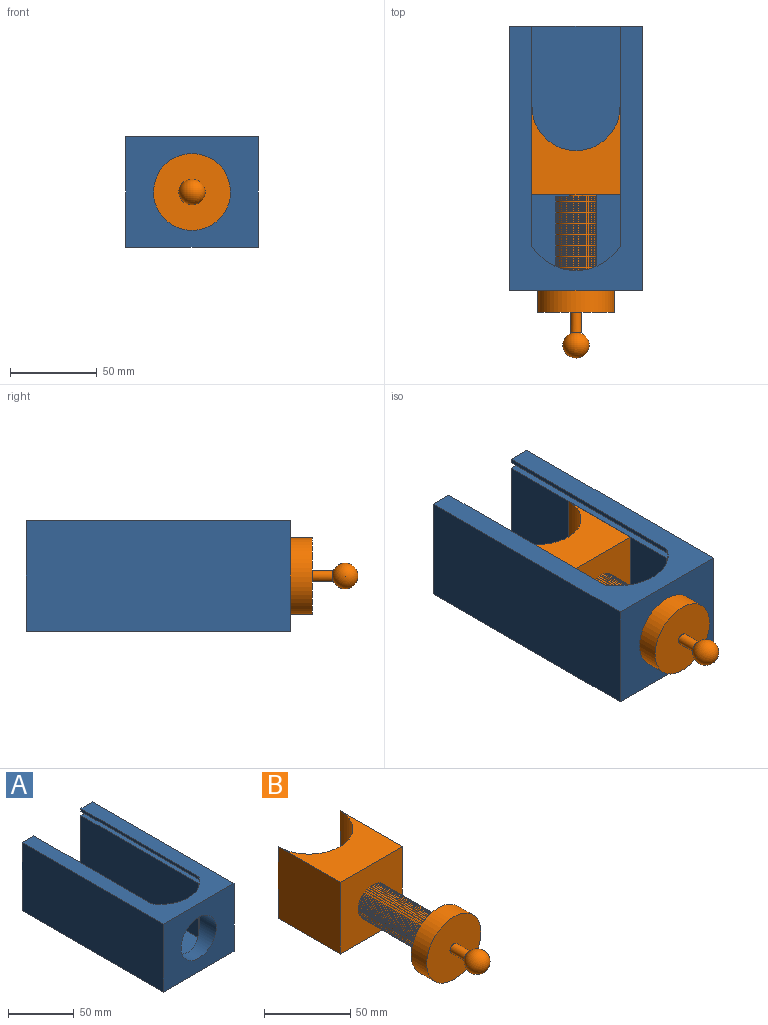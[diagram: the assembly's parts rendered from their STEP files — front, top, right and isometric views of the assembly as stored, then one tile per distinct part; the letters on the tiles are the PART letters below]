
ASSEMBLY  parts=2 mates=1
PART A: 19 faces, bbox 76.2x152.4x63.5 mm
  f0: plane 76.2x63.5mm, normal (0,1,0), area 1886.4mm2, adj f1,f3,f4,f6,f7,f8,f9,f11
  f1: plane 127x2.54mm, normal (1,0,0), area 322.6mm2, adj f0,f2,f4,f17
  f2: cylinder r=29.87mm len=50.8mm, axis (0,0,1), area 154.3mm2, adj f1,f3,f4,f17
  f3: plane 127x2.54mm, normal (-1,0,0), area 322.6mm2, adj f0,f2,f4,f17
  f4: plane 152.4x76.2mm, normal (0,0,1), area 4653.4mm2, adj f0,f1,f2,f3,f5,f6,f7
  f5: plane 76.2x63.5mm, normal (0,-1,0), area 3698.6mm2, adj f4,f6,f7,f8,f13
  f6: plane 152.4x63.5mm, normal (1,0,0), area 9677.4mm2, adj f0,f4,f5,f8
  f7: plane 152.4x63.5mm, normal (-1,0,0), area 9677.4mm2, adj f0,f4,f5,f8
  f8: plane 152.4x76.2mm, normal (0,0,-1), area 11612.9mm2, adj f0,f5,f6,f7
  f9: plane 127x50.75mm, normal (1,0,0), area 6444.9mm2, adj f0,f10,f12,f15
  f10: cylinder r=29.87mm len=50.8mm, axis (0,0,1), area 1874mm2, adj f9,f11,f12,f13,f15
  f11: plane 127x50.75mm, normal (-1,0,0), area 6444.9mm2, adj f0,f10,f12,f15
  f12: plane 141.15x50.8mm, normal (0,0,1), area 6959.5mm2, adj f0,f9,f10,f11
  f13: cylinder r=19.05mm len=38.1mm, axis (0,-1,0), area 1743.5mm2, adj f5,f10
  f14: plane 145.03x3.86mm, normal (-1,0,0), area 560.2mm2, adj f0,f15,f17,f18
  f15: plane 145.03x63.5mm, normal (0,0,1), area 2250.2mm2, adj f0,f9,f10,f11,f14,f16,f18
  f16: plane 145.03x3.86mm, normal (1,0,0), area 560.2mm2, adj f0,f15,f17,f18
  f17: plane 145.03x63.5mm, normal (0,0,-1), area 2250.2mm2, adj f0,f1,f2,f3,f14,f16,f18
  f18: plane 63.5x3.86mm, normal (0,1,0), area 245.3mm2, adj f14,f15,f16,f17
PART B: 189 faces, bbox 50.8x137.7x50.8 mm
  f0: plane 55.12x7.77mm, normal (0,0,1), area 390.6mm2, adj f1,f2,f3,f4,f5,f6,f7,f8
  f1: plane 23.16x23.16mm, normal (0,1,0), area 81.9mm2, adj f0,f132,f133,f134
  f2: plane 55.12x4.13mm, normal (1,0,0), area 227.7mm2, adj f0,f3,f133,f134,f135,f136,f137,f138
  f3: plane 50.8x50.8mm, normal (0,-1,0), area 2498.6mm2, adj f0,f2,f4,f134,f178,f179,f180,f181
  f4: cylinder r=3.81mm len=55.12mm, axis (0,-1,0), area 989.6mm2, adj f0,f3,f5,f178
  f5: plane 20.62x20.62mm, normal (0,1,0), area 258.4mm2, adj f0,f4,f6,f134,f178
  f6: cylinder r=10.31mm len=20.62mm, axis (0,1,0), area 41.8mm2, adj f0,f5,f7,f134
  f7: plane 23.16x23.16mm, normal (0,1,0), area 81.9mm2, adj f0,f6,f134,f176
  f8: plane 23.16x23.16mm, normal (0,-1,0), area 81.9mm2, adj f0,f9,f134,f175
  f9: cylinder r=10.31mm len=20.62mm, axis (0,1,0), area 41.8mm2, adj f0,f8,f10,f134
  f10: plane 23.16x23.16mm, normal (0,1,0), area 81.9mm2, adj f0,f9,f134,f175
  f11: plane 23.16x23.16mm, normal (0,-1,0), area 81.9mm2, adj f0,f12,f134,f174
  f12: cylinder r=10.31mm len=20.62mm, axis (0,1,0), area 41.8mm2, adj f0,f11,f13,f134
  f13: plane 23.16x23.16mm, normal (0,1,0), area 81.9mm2, adj f0,f12,f134,f174
  f14: plane 23.16x23.16mm, normal (0,-1,0), area 81.9mm2, adj f0,f15,f134,f173
  f15: cylinder r=10.31mm len=20.62mm, axis (0,1,0), area 41.8mm2, adj f0,f14,f16,f134
  f16: plane 23.16x23.16mm, normal (0,1,0), area 81.9mm2, adj f0,f15,f134,f173
  f17: plane 23.16x23.16mm, normal (0,-1,0), area 81.9mm2, adj f0,f18,f134,f172
  f18: cylinder r=10.31mm len=20.62mm, axis (0,1,0), area 41.8mm2, adj f0,f17,f19,f134
  f19: plane 23.16x23.16mm, normal (0,1,0), area 81.9mm2, adj f0,f18,f134,f172
  f20: plane 23.16x23.16mm, normal (0,-1,0), area 81.9mm2, adj f0,f21,f134,f171
  f21: cylinder r=10.31mm len=20.62mm, axis (0,1,0), area 41.8mm2, adj f0,f20,f22,f134
  f22: plane 23.16x23.16mm, normal (0,1,0), area 81.9mm2, adj f0,f21,f134,f171
  f23: plane 23.16x23.16mm, normal (0,-1,0), area 81.9mm2, adj f0,f24,f134,f170
  f24: cylinder r=10.31mm len=20.62mm, axis (0,1,0), area 41.8mm2, adj f0,f23,f25,f134
  f25: plane 23.16x23.16mm, normal (0,1,0), area 81.9mm2, adj f0,f24,f134,f170
  f26: plane 23.16x23.16mm, normal (0,-1,0), area 81.9mm2, adj f0,f27,f134,f169
  f27: cylinder r=10.31mm len=20.62mm, axis (0,1,0), area 41.8mm2, adj f0,f26,f28,f134
  f28: plane 23.16x23.16mm, normal (0,1,0), area 81.9mm2, adj f0,f27,f134,f169
  f29: plane 23.16x23.16mm, normal (0,-1,0), area 81.9mm2, adj f0,f30,f134,f168
  f30: cylinder r=10.31mm len=20.62mm, axis (0,1,0), area 41.8mm2, adj f0,f29,f31,f134
  f31: plane 23.16x23.16mm, normal (0,1,0), area 81.9mm2, adj f0,f30,f134,f168
  f32: plane 23.16x23.16mm, normal (0,-1,0), area 81.9mm2, adj f0,f33,f134,f167
  f33: cylinder r=10.31mm len=20.62mm, axis (0,1,0), area 41.8mm2, adj f0,f32,f34,f134
  f34: plane 23.16x23.16mm, normal (0,1,0), area 81.9mm2, adj f0,f33,f134,f167
  f35: plane 23.16x23.16mm, normal (0,-1,0), area 81.9mm2, adj f0,f36,f134,f166
  f36: cylinder r=10.31mm len=20.62mm, axis (0,1,0), area 41.8mm2, adj f0,f35,f37,f134
  f37: plane 23.16x23.16mm, normal (0,1,0), area 81.9mm2, adj f0,f36,f134,f166
  f38: plane 23.16x23.16mm, normal (0,-1,0), area 81.9mm2, adj f0,f39,f134,f165
  f39: cylinder r=10.31mm len=20.62mm, axis (0,1,0), area 41.8mm2, adj f0,f38,f40,f134
  f40: plane 23.16x23.16mm, normal (0,1,0), area 81.9mm2, adj f0,f39,f134,f165
  f41: plane 23.16x23.16mm, normal (0,-1,0), area 81.9mm2, adj f0,f42,f134,f164
  f42: cylinder r=10.31mm len=20.62mm, axis (0,1,0), area 41.8mm2, adj f0,f41,f43,f134
  f43: plane 23.16x23.16mm, normal (0,1,0), area 81.9mm2, adj f0,f42,f134,f164
  f44: plane 23.16x23.16mm, normal (0,-1,0), area 81.9mm2, adj f0,f45,f134,f163
  f45: cylinder r=10.31mm len=20.62mm, axis (0,1,0), area 41.8mm2, adj f0,f44,f46,f134
  f46: plane 23.16x23.16mm, normal (0,1,0), area 81.9mm2, adj f0,f45,f134,f163
  f47: plane 23.16x23.16mm, normal (0,-1,0), area 81.9mm2, adj f0,f48,f134,f162
  f48: cylinder r=10.31mm len=20.62mm, axis (0,1,0), area 41.8mm2, adj f0,f47,f49,f134
  f49: plane 23.16x23.16mm, normal (0,1,0), area 81.9mm2, adj f0,f48,f134,f162
  f50: plane 23.16x23.16mm, normal (0,-1,0), area 81.9mm2, adj f0,f51,f134,f161
  f51: cylinder r=10.31mm len=20.62mm, axis (0,1,0), area 41.8mm2, adj f0,f50,f52,f134
  f52: plane 23.16x23.16mm, normal (0,1,0), area 81.9mm2, adj f0,f51,f134,f161
  f53: plane 23.16x23.16mm, normal (0,-1,0), area 81.9mm2, adj f0,f54,f134,f160
  f54: cylinder r=10.31mm len=20.62mm, axis (0,1,0), area 41.8mm2, adj f0,f53,f55,f134
  f55: plane 23.16x23.16mm, normal (0,1,0), area 81.9mm2, adj f0,f54,f134,f160
  f56: plane 23.16x23.16mm, normal (0,-1,0), area 81.9mm2, adj f0,f57,f134,f159
  f57: cylinder r=10.31mm len=20.62mm, axis (0,1,0), area 41.8mm2, adj f0,f56,f58,f134
  f58: plane 23.16x23.16mm, normal (0,1,0), area 81.9mm2, adj f0,f57,f134,f159
  f59: plane 23.16x23.16mm, normal (0,-1,0), area 81.9mm2, adj f0,f60,f134,f158
  f60: cylinder r=10.31mm len=20.62mm, axis (0,1,0), area 41.8mm2, adj f0,f59,f61,f134
  f61: plane 23.16x23.16mm, normal (0,1,0), area 81.9mm2, adj f0,f60,f134,f158
  f62: plane 23.16x23.16mm, normal (0,-1,0), area 81.9mm2, adj f0,f63,f134,f157
  f63: cylinder r=10.31mm len=20.62mm, axis (0,1,0), area 41.8mm2, adj f0,f62,f64,f134
  f64: plane 23.16x23.16mm, normal (0,1,0), area 81.9mm2, adj f0,f63,f134,f157
  f65: plane 23.16x23.16mm, normal (0,-1,0), area 81.9mm2, adj f0,f66,f134,f156
  f66: cylinder r=10.31mm len=20.62mm, axis (0,1,0), area 41.8mm2, adj f0,f65,f67,f134
  f67: plane 23.16x23.16mm, normal (0,1,0), area 81.9mm2, adj f0,f66,f134,f156
  f68: plane 23.16x23.16mm, normal (0,-1,0), area 81.9mm2, adj f0,f69,f134,f155
  f69: cylinder r=10.31mm len=20.62mm, axis (0,1,0), area 41.8mm2, adj f0,f68,f70,f134
  f70: plane 23.16x23.16mm, normal (0,1,0), area 81.9mm2, adj f0,f69,f134,f155
  f71: plane 23.16x23.16mm, normal (0,-1,0), area 81.9mm2, adj f0,f72,f134,f154
  f72: cylinder r=10.31mm len=20.62mm, axis (0,1,0), area 41.8mm2, adj f0,f71,f73,f134
  f73: plane 23.16x23.16mm, normal (0,1,0), area 81.9mm2, adj f0,f72,f134,f154
  f74: plane 23.16x23.16mm, normal (0,-1,0), area 81.9mm2, adj f0,f75,f134,f153
  f75: cylinder r=10.31mm len=20.62mm, axis (0,1,0), area 41.8mm2, adj f0,f74,f76,f134
  f76: plane 23.16x23.16mm, normal (0,1,0), area 81.9mm2, adj f0,f75,f134,f153
  f77: plane 23.16x23.16mm, normal (0,-1,0), area 81.9mm2, adj f0,f78,f134,f152
  f78: cylinder r=10.31mm len=20.62mm, axis (0,1,0), area 41.8mm2, adj f0,f77,f79,f134
  f79: plane 23.16x23.16mm, normal (0,1,0), area 81.9mm2, adj f0,f78,f134,f152
  f80: plane 23.16x23.16mm, normal (0,-1,0), area 81.9mm2, adj f0,f81,f134,f151
  f81: cylinder r=10.31mm len=20.62mm, axis (0,1,0), area 41.8mm2, adj f0,f80,f82,f134
  f82: plane 23.16x23.16mm, normal (0,1,0), area 81.9mm2, adj f0,f81,f134,f151
  f83: plane 23.16x23.16mm, normal (0,-1,0), area 81.9mm2, adj f0,f84,f134,f150
  f84: cylinder r=10.31mm len=20.62mm, axis (0,1,0), area 41.8mm2, adj f0,f83,f85,f134
  f85: plane 23.16x23.16mm, normal (0,1,0), area 81.9mm2, adj f0,f84,f134,f150
  f86: plane 23.16x23.16mm, normal (0,-1,0), area 81.9mm2, adj f0,f87,f134,f149
  f87: cylinder r=10.31mm len=20.62mm, axis (0,1,0), area 41.8mm2, adj f0,f86,f88,f134
  f88: plane 23.16x23.16mm, normal (0,1,0), area 81.9mm2, adj f0,f87,f134,f149
  f89: plane 23.16x23.16mm, normal (0,-1,0), area 81.9mm2, adj f0,f90,f134,f148
  f90: cylinder r=10.31mm len=20.62mm, axis (0,1,0), area 41.8mm2, adj f0,f89,f91,f134
  f91: plane 23.16x23.16mm, normal (0,1,0), area 81.9mm2, adj f0,f90,f134,f148
  f92: plane 23.16x23.16mm, normal (0,-1,0), area 81.9mm2, adj f0,f93,f134,f147
  f93: cylinder r=10.31mm len=20.62mm, axis (0,1,0), area 41.8mm2, adj f0,f92,f94,f134
  f94: plane 23.16x23.16mm, normal (0,1,0), area 81.9mm2, adj f0,f93,f134,f147
  f95: plane 23.16x23.16mm, normal (0,-1,0), area 81.9mm2, adj f0,f96,f134,f146
  f96: cylinder r=10.31mm len=20.62mm, axis (0,1,0), area 41.8mm2, adj f0,f95,f97,f134
  f97: plane 23.16x23.16mm, normal (0,1,0), area 81.9mm2, adj f0,f96,f134,f146
  f98: plane 23.16x23.16mm, normal (0,-1,0), area 81.9mm2, adj f0,f99,f134,f145
  f99: cylinder r=10.31mm len=20.62mm, axis (0,1,0), area 41.8mm2, adj f0,f98,f100,f134
  f100: plane 23.16x23.16mm, normal (0,1,0), area 81.9mm2, adj f0,f99,f134,f145
  f101: plane 23.16x23.16mm, normal (0,-1,0), area 81.9mm2, adj f0,f102,f134,f144
  f102: cylinder r=10.31mm len=20.62mm, axis (0,1,0), area 41.8mm2, adj f0,f101,f103,f134
  f103: plane 23.16x23.16mm, normal (0,1,0), area 81.9mm2, adj f0,f102,f134,f144
  f104: plane 23.16x23.16mm, normal (0,-1,0), area 81.9mm2, adj f0,f105,f134,f143
  f105: cylinder r=10.31mm len=20.62mm, axis (0,1,0), area 41.8mm2, adj f0,f104,f106,f134
  f106: plane 23.16x23.16mm, normal (0,1,0), area 81.9mm2, adj f0,f105,f134,f143
  f107: plane 23.16x23.16mm, normal (0,-1,0), area 81.9mm2, adj f0,f108,f134,f142
  f108: cylinder r=10.31mm len=20.62mm, axis (0,1,0), area 41.8mm2, adj f0,f107,f109,f134
  f109: plane 23.16x23.16mm, normal (0,1,0), area 81.9mm2, adj f0,f108,f134,f142
  f110: plane 23.16x23.16mm, normal (0,-1,0), area 81.9mm2, adj f0,f111,f134,f141
  f111: cylinder r=10.31mm len=20.62mm, axis (0,1,0), area 41.8mm2, adj f0,f110,f112,f134
  f112: plane 23.16x23.16mm, normal (0,1,0), area 81.9mm2, adj f0,f111,f134,f141
  f113: plane 23.16x23.16mm, normal (0,-1,0), area 81.9mm2, adj f0,f114,f134,f140
  f114: cylinder r=10.31mm len=20.62mm, axis (0,1,0), area 41.8mm2, adj f0,f113,f115,f134
  f115: plane 23.16x23.16mm, normal (0,1,0), area 81.9mm2, adj f0,f114,f134,f140
  f116: plane 23.16x23.16mm, normal (0,-1,0), area 81.9mm2, adj f0,f117,f134,f139
  f117: cylinder r=10.31mm len=20.62mm, axis (0,1,0), area 41.8mm2, adj f0,f116,f118,f134
  f118: plane 23.16x23.16mm, normal (0,1,0), area 81.9mm2, adj f0,f117,f134,f139
  f119: plane 23.16x23.16mm, normal (0,-1,0), area 81.9mm2, adj f0,f120,f134,f138
  f120: cylinder r=10.31mm len=20.62mm, axis (0,1,0), area 41.8mm2, adj f0,f119,f121,f134
  f121: plane 23.16x23.16mm, normal (0,1,0), area 81.9mm2, adj f0,f120,f134,f138
  f122: plane 23.16x23.16mm, normal (0,-1,0), area 81.9mm2, adj f0,f123,f134,f137
  f123: cylinder r=10.31mm len=20.62mm, axis (0,1,0), area 41.8mm2, adj f0,f122,f124,f134
  f124: plane 23.16x23.16mm, normal (0,1,0), area 81.9mm2, adj f0,f123,f134,f137
  f125: plane 23.16x23.16mm, normal (0,-1,0), area 81.9mm2, adj f0,f126,f134,f136
  f126: cylinder r=10.31mm len=20.62mm, axis (0,1,0), area 41.8mm2, adj f0,f125,f127,f134
  f127: plane 23.16x23.16mm, normal (0,1,0), area 81.9mm2, adj f0,f126,f134,f136
  f128: plane 23.16x23.16mm, normal (0,-1,0), area 81.9mm2, adj f0,f129,f134,f135
  f129: cylinder r=10.31mm len=20.62mm, axis (0,1,0), area 41.8mm2, adj f0,f128,f130,f134
  f130: plane 23.16x23.16mm, normal (0,1,0), area 81.9mm2, adj f0,f129,f134,f135
  f131: plane 23.16x23.16mm, normal (0,-1,0), area 81.9mm2, adj f0,f132,f133,f134
  f132: cylinder r=10.31mm len=20.62mm, axis (0,1,0), area 41.8mm2, adj f0,f1,f131,f134
  f133: cylinder r=11.58mm len=23.16mm, axis (0,1,0), area 47.3mm2, adj f1,f2,f131,f134
  f134: plane 55.12x11.58mm, normal (0,0,-1), area 597.6mm2, adj f1,f2,f3,f5,f6,f7,f8,f9
  f135: cylinder r=11.58mm len=23.16mm, axis (0,1,0), area 47.3mm2, adj f2,f128,f130,f134
  f136: cylinder r=11.58mm len=23.16mm, axis (0,1,0), area 47.3mm2, adj f2,f125,f127,f134
  f137: cylinder r=11.58mm len=23.16mm, axis (0,1,0), area 47.3mm2, adj f2,f122,f124,f134
  f138: cylinder r=11.58mm len=23.16mm, axis (0,1,0), area 47.3mm2, adj f2,f119,f121,f134
  f139: cylinder r=11.58mm len=23.16mm, axis (0,1,0), area 47.3mm2, adj f2,f116,f118,f134
  f140: cylinder r=11.58mm len=23.16mm, axis (0,1,0), area 47.3mm2, adj f2,f113,f115,f134
  f141: cylinder r=11.58mm len=23.16mm, axis (0,1,0), area 47.3mm2, adj f2,f110,f112,f134
  f142: cylinder r=11.58mm len=23.16mm, axis (0,1,0), area 47.3mm2, adj f2,f107,f109,f134
  f143: cylinder r=11.58mm len=23.16mm, axis (0,1,0), area 47.3mm2, adj f2,f104,f106,f134
  f144: cylinder r=11.58mm len=23.16mm, axis (0,1,0), area 47.3mm2, adj f2,f101,f103,f134
  f145: cylinder r=11.58mm len=23.16mm, axis (0,1,0), area 47.3mm2, adj f2,f98,f100,f134
  f146: cylinder r=11.58mm len=23.16mm, axis (0,1,0), area 47.3mm2, adj f2,f95,f97,f134
  f147: cylinder r=11.58mm len=23.16mm, axis (0,1,0), area 47.3mm2, adj f2,f92,f94,f134
  f148: cylinder r=11.58mm len=23.16mm, axis (0,1,0), area 47.3mm2, adj f2,f89,f91,f134
  f149: cylinder r=11.58mm len=23.16mm, axis (0,1,0), area 47.3mm2, adj f2,f86,f88,f134
  f150: cylinder r=11.58mm len=23.16mm, axis (0,1,0), area 47.3mm2, adj f2,f83,f85,f134
  f151: cylinder r=11.58mm len=23.16mm, axis (0,1,0), area 47.3mm2, adj f2,f80,f82,f134
  f152: cylinder r=11.58mm len=23.16mm, axis (0,1,0), area 47.3mm2, adj f2,f77,f79,f134
  f153: cylinder r=11.58mm len=23.16mm, axis (0,1,0), area 47.3mm2, adj f2,f74,f76,f134
  f154: cylinder r=11.58mm len=23.16mm, axis (0,1,0), area 47.3mm2, adj f2,f71,f73,f134
  f155: cylinder r=11.58mm len=23.16mm, axis (0,1,0), area 47.3mm2, adj f2,f68,f70,f134
  f156: cylinder r=11.58mm len=23.16mm, axis (0,1,0), area 47.3mm2, adj f2,f65,f67,f134
  f157: cylinder r=11.58mm len=23.16mm, axis (0,1,0), area 47.3mm2, adj f2,f62,f64,f134
  f158: cylinder r=11.58mm len=23.16mm, axis (0,1,0), area 47.3mm2, adj f2,f59,f61,f134
  f159: cylinder r=11.58mm len=23.16mm, axis (0,1,0), area 47.3mm2, adj f2,f56,f58,f134
  f160: cylinder r=11.58mm len=23.16mm, axis (0,1,0), area 47.3mm2, adj f2,f53,f55,f134
  f161: cylinder r=11.58mm len=23.16mm, axis (0,1,0), area 47.3mm2, adj f2,f50,f52,f134
  f162: cylinder r=11.58mm len=23.16mm, axis (0,1,0), area 47.3mm2, adj f2,f47,f49,f134
  f163: cylinder r=11.58mm len=23.16mm, axis (0,1,0), area 47.3mm2, adj f2,f44,f46,f134
  f164: cylinder r=11.58mm len=23.16mm, axis (0,1,0), area 47.3mm2, adj f2,f41,f43,f134
  f165: cylinder r=11.58mm len=23.16mm, axis (0,1,0), area 47.3mm2, adj f2,f38,f40,f134
  f166: cylinder r=11.58mm len=23.16mm, axis (0,1,0), area 47.3mm2, adj f2,f35,f37,f134
  f167: cylinder r=11.58mm len=23.16mm, axis (0,1,0), area 47.3mm2, adj f2,f32,f34,f134
  f168: cylinder r=11.58mm len=23.16mm, axis (0,1,0), area 47.3mm2, adj f2,f29,f31,f134
  f169: cylinder r=11.58mm len=23.16mm, axis (0,1,0), area 47.3mm2, adj f2,f26,f28,f134
  f170: cylinder r=11.58mm len=23.16mm, axis (0,1,0), area 47.3mm2, adj f2,f23,f25,f134
  f171: cylinder r=11.58mm len=23.16mm, axis (0,1,0), area 47.3mm2, adj f2,f20,f22,f134
  f172: cylinder r=11.58mm len=23.16mm, axis (0,1,0), area 47.3mm2, adj f2,f17,f19,f134
  f173: cylinder r=11.58mm len=23.16mm, axis (0,1,0), area 47.3mm2, adj f2,f14,f16,f134
  f174: cylinder r=11.58mm len=23.16mm, axis (0,1,0), area 47.3mm2, adj f2,f11,f13,f134
  f175: cylinder r=11.58mm len=23.16mm, axis (0,1,0), area 47.3mm2, adj f2,f8,f10,f134
  f176: cylinder r=11.58mm len=23.16mm, axis (0,1,0), area 47.3mm2, adj f2,f7,f134,f177
  f177: plane 44.45x44.45mm, normal (0,1,0), area 1129.5mm2, adj f2,f134,f176,f183
  f178: plane 55.12x0.32mm, normal (-1,0,0), area 17.7mm2, adj f3,f4,f5,f134
  f179: plane 50.8x50.8mm, normal (-1,0,0), area 2580.6mm2, adj f3,f180,f182,f184
  f180: plane 50.8x50.8mm, normal (0,0,-1), area 1567.2mm2, adj f3,f179,f181,f184
  f181: plane 50.8x50.8mm, normal (1,0,0), area 2580.6mm2, adj f3,f180,f182,f184
  f182: plane 50.8x50.8mm, normal (0,0,1), area 1567.2mm2, adj f3,f179,f181,f184
  f183: cylinder r=22.23mm len=44.45mm, axis (0,-1,0), area 1773.5mm2, adj f177,f185
  f184: cylinder r=25.4mm len=50.8mm, axis (0,0,-1), area 4053.7mm2, adj f179,f180,f181,f182
  f185: plane 44.45x44.45mm, normal (0,-1,0), area 1520.1mm2, adj f183,f186
  f186: cylinder r=3.17mm len=11.91mm, axis (0,-1,0), area 237.4mm2, adj f185,f187
  f187: torus R=0.2mm, axis (1,0,0), area 33.1mm2, adj f186
  f188: torus R=0.2mm, axis (1,0,0), area 699.7mm2
PLACE A t=(-39.15,-12.43,-16.49)mm
PLACE B t=(-39.15,-120.38,15.26)mm
MATE slider B.f183 <-> A.f13  axis (0,1,0) through (-39.15,-88.63,15.26)mm
